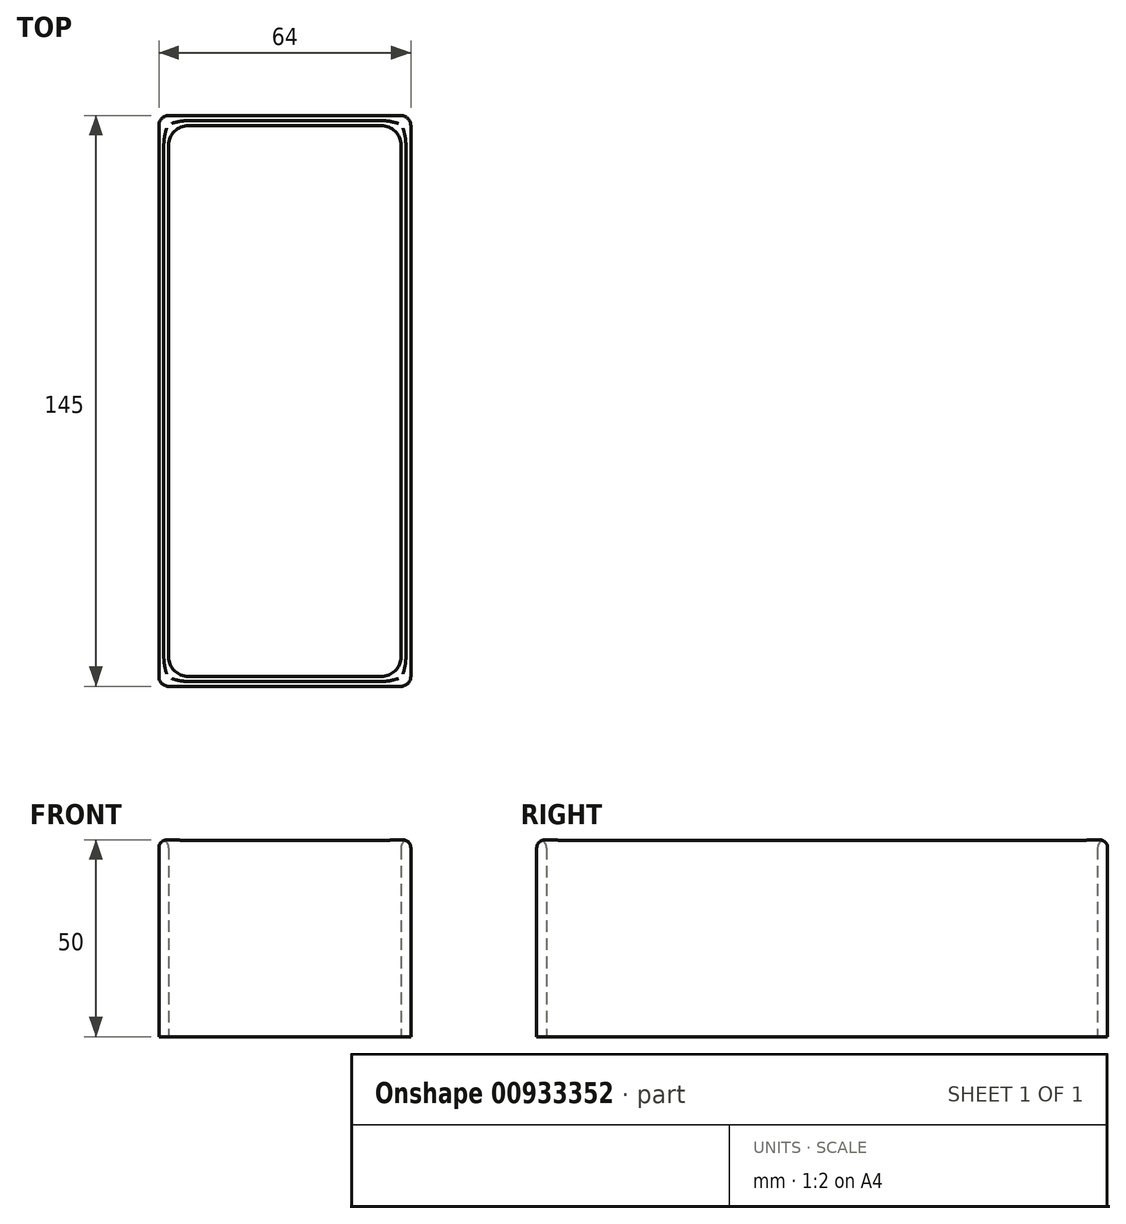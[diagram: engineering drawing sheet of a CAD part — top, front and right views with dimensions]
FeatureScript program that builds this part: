
annotation { "Feature Type Name" : "Feature", "Feature Type Description" : "" }
export const myFeature = defineFeature(function(context is Context, id is Id, definition is map)
    precondition{}
    {
        {
            var Q0;
            Q0=qCreatedBy(makeId("Top.planeOp"),FACE);
            var sketch = newSketch(context, id + "F0", { "sketchPlane" : qUnion([Q0])});
            skLineSegment(sketch, "E0.bottom", {"start": v(29.5, -72.5) * mm, "end": v(-29.5, -72.5) * mm});
            skLineSegment(sketch, "E0.top", {"start": v(29.5, 72.5) * mm, "end": v(-29.5, 72.5) * mm});
            skLineSegment(sketch, "E0.left", {"start": v(32, -70) * mm, "end": v(32, 70) * mm});
            skLineSegment(sketch, "E0.right", {"start": v(-32, -70) * mm, "end": v(-32, 70) * mm});
            skPoint(sketch, "E0.middle", {"position": v(0, 0) * mm});
            skLineSegment(sketch, "E1.bottom", {"start": v(29.5, -70) * mm, "end": v(-29.5, -70) * mm});
            skLineSegment(sketch, "E1.top", {"start": v(29.5, 70) * mm, "end": v(-29.5, 70) * mm});
            skLineSegment(sketch, "E1.left", {"start": v(29.5, -70) * mm, "end": v(29.5, 70) * mm});
            skLineSegment(sketch, "E1.right", {"start": v(-29.5, -70) * mm, "end": v(-29.5, 70) * mm});
            skPoint(sketch, "E2.visualSharp", {"position": v(-32, -72.5) * mm});
            skArc(sketch, "E2.filletArc", {"start": v(-32, -70) * mm, "mid": v(-31.27, -71.77) * mm, "end": v(-29.5, -72.5) * mm});
            skPoint(sketch, "E3.visualSharp", {"position": v(32, -72.5) * mm});
            skArc(sketch, "E3.filletArc", {"start": v(29.5, -72.5) * mm, "mid": v(31.27, -71.77) * mm, "end": v(32, -70) * mm});
            skPoint(sketch, "E4.visualSharp", {"position": v(32, 72.5) * mm});
            skArc(sketch, "E4.filletArc", {"start": v(32, 70) * mm, "mid": v(31.27, 71.77) * mm, "end": v(29.5, 72.5) * mm});
            skPoint(sketch, "E5.visualSharp", {"position": v(-32, 72.5) * mm});
            skArc(sketch, "E5.filletArc", {"start": v(-29.5, 72.5) * mm, "mid": v(-31.27, 71.77) * mm, "end": v(-32, 70) * mm});
            skSolve(sketch);
        }
        {
            var Q0;
            Q0=makeQuery(id+"F0.imprint","IMPRINT",FACE,{"disambiguationData":[TD([[makeQuery(id+"F0.imprint","IMPRINT",EDGE,{"derivedFrom":sQuery(id+"F0.wireOp",EDGE,"E0.bottom")}),-1.0]])]});
            extrude(context, id + "F1", {"entities" : qUnion([Q0]), "depth" : 50 * mm, "offsetDistance" : 25 * mm});
        }
        {
            var Q0;
            Q0=makeQuery(id+"F1.opExtrude","SWEPT_EDGE",EDGE,{"disambiguationData":[OSD([sQuery(id+"F0.wireOp",EDGE,"E1.top"),sQuery(id+"F0.wireOp",EDGE,"E1.right")])]});
            var Q1;
            Q1=makeQuery(id+"F1.opExtrude","SWEPT_EDGE",EDGE,{"disambiguationData":[OSD([sQuery(id+"F0.wireOp",EDGE,"E1.top"),sQuery(id+"F0.wireOp",EDGE,"E1.left")])]});
            var Q2;
            Q2=makeQuery(id+"F1.opExtrude","SWEPT_EDGE",EDGE,{"disambiguationData":[OSD([sQuery(id+"F0.wireOp",EDGE,"E1.bottom"),sQuery(id+"F0.wireOp",EDGE,"E1.right")])]});
            var Q3;
            Q3=makeQuery(id+"F1.opExtrude","SWEPT_EDGE",EDGE,{"disambiguationData":[OSD([sQuery(id+"F0.wireOp",EDGE,"E1.bottom"),sQuery(id+"F0.wireOp",EDGE,"E1.left")])]});
            fillet(context, id + "F2", {"entities" : qUnion([Q0, Q1, Q2, Q3]), "radius" : 5 * mm, "tangentPropagation" : true, "allowEdgeOverflow" : false});
        }
        {
            var Q0;
            Q0=makeQuery(id+"F1.opExtrude","CAP_FACE",FACE,{"disambiguationData":[OSD([sQuery(id+"F0.wireOp",EDGE,"E0.bottom"),sQuery(id+"F0.wireOp",EDGE,"E0.top"),sQuery(id+"F0.wireOp",EDGE,"E0.left"),sQuery(id+"F0.wireOp",EDGE,"E0.right"),sQuery(id+"F0.wireOp",EDGE,"E1.bottom"),sQuery(id+"F0.wireOp",EDGE,"E1.top"),sQuery(id+"F0.wireOp",EDGE,"E1.left"),sQuery(id+"F0.wireOp",EDGE,"E1.right"),sQuery(id+"F0.wireOp",EDGE,"E2.filletArc"),sQuery(id+"F0.wireOp",EDGE,"E3.filletArc"),sQuery(id+"F0.wireOp",EDGE,"E4.filletArc"),sQuery(id+"F0.wireOp",EDGE,"E5.filletArc")])],"isStart":false});
            fillet(context, id + "F3", {"entities" : qUnion([Q0]), "radius" : 2 * mm, "tangentPropagation" : true, "allowEdgeOverflow" : false});
        }
    });
